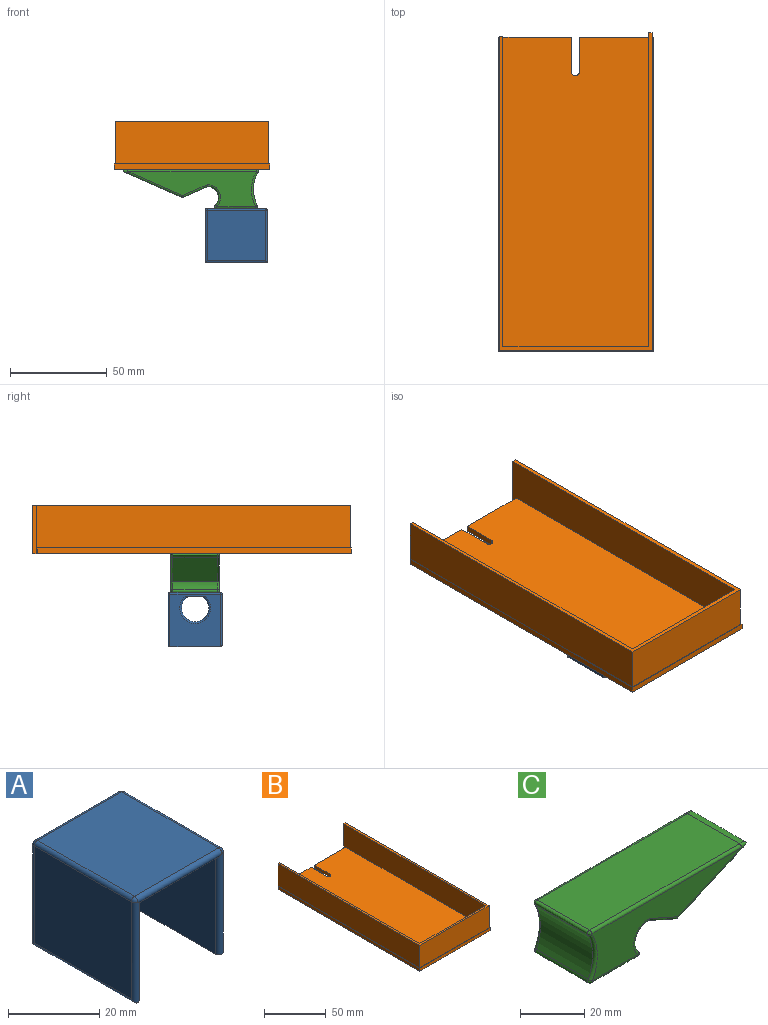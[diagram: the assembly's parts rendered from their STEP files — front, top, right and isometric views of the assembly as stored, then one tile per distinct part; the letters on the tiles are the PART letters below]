
ASSEMBLY  parts=3 mates=2
PART A: 25 faces, bbox 28x32x28.1 mm
  f0: plane 27x26mm, normal (0,1,0), area 513.9mm2, adj f1,f5,f10,f15,f20,f21
  f1: plane 32x27mm, normal (0,0,-1), area 167.1mm2, adj f0,f2,f3,f4,f6,f12,f13,f16
  f2: plane 26x24mm, normal (0,-1,0), area 435.9mm2, adj f1,f3,f4,f5,f11
  f3: plane 28x26mm, normal (1,0,0), area 728mm2, adj f1,f2,f5,f13
  f4: plane 28x26mm, normal (-1,0,0), area 728mm2, adj f1,f2,f5,f16
  f5: plane 31x24mm, normal (0,0,-1), area 693.7mm2, adj f0,f2,f3,f4,f9,f10,f11,f17
  f6: plane 30x27mm, normal (1,0,0), area 810mm2, adj f1,f16,f21,f24
  f7: plane 30x26mm, normal (0,0,1), area 780mm2, adj f14,f17,f20,f24
  f8: plane 30x26mm, normal (-1,0,0), area 780mm2, adj f12,f13,f14,f15
  f9: cylinder r=7mm len=14mm, axis (0,-1,0), area 37mm2, adj f5,f10,f11
  f10: torus R=8mm, axis (0,-1,0), area 59.3mm2, adj f0,f5,f9
  f11: torus R=8mm, axis (0,-1,0), area 59.3mm2, adj f2,f5,f9
  f12: cylinder r=1mm len=32mm, axis (0,1,0), area 49.1mm2, adj f1,f8,f13,f15
  f13: cylinder r=1mm len=27mm, axis (0,0,-1), area 83.3mm2, adj f1,f3,f8,f12,f17,f18
  f14: cylinder r=1mm len=30mm, axis (0,-1,0), area 47.1mm2, adj f7,f8,f18,f19
  f15: cylinder r=1mm len=27mm, axis (0,0,-1), area 41.8mm2, adj f0,f8,f12,f19
  f16: cylinder r=1mm len=27mm, axis (0,0,1), area 83.8mm2, adj f1,f4,f6,f17,f22
  f17: cylinder r=1mm len=26mm, axis (-1,0,0), area 79.7mm2, adj f5,f7,f13,f16,f18,f22
  f18: sphere r=1mm, area 1.6mm2, adj f13,f14,f17
  f19: sphere r=1mm, area 1.6mm2, adj f14,f15,f20
  f20: cylinder r=1mm len=26mm, axis (-1,0,0), area 40.8mm2, adj f0,f7,f19,f23
  f21: cylinder r=1mm len=27mm, axis (0,0,1), area 42.4mm2, adj f0,f1,f6,f23
  f22: sphere r=1mm, area 1.6mm2, adj f16,f17,f24
  f23: sphere r=1mm, area 1.6mm2, adj f20,f21,f24
  f24: cylinder r=1mm len=30mm, axis (0,1,0), area 47.1mm2, adj f6,f7,f22,f23
PART B: 22 faces, bbox 80x164.5x25 mm
  f0: plane 35.36x3mm, normal (0,1,0), area 106.1mm2, adj f3,f9,f15,f20
  f1: plane 35.64x3mm, normal (0,1,0), area 106.9mm2, adj f3,f9,f13,f21
  f2: plane 3x0.33mm, normal (0,1,0), area 1mm2, adj f5,f8,f9,f17
  f3: plane 159.54x75mm, normal (0,0,1), area 11887.6mm2, adj f0,f1,f13,f14,f15,f19,f20,f21
  f4: plane 3x0.67mm, normal (0,1,0), area 2mm2, adj f7,f8,f9,f11
  f5: plane 162x3mm, normal (-1,0,0), area 486mm2, adj f2,f6,f8,f9
  f6: plane 80x3mm, normal (0,-1,0), area 240mm2, adj f5,f7,f8,f9
  f7: plane 162x3mm, normal (1,0,0), area 486mm2, adj f4,f6,f8,f9
  f8: plane 162x80mm, normal (0,0,1), area 198.6mm2, adj f2,f4,f5,f6,f7,f10,f11,f17
  f9: plane 164.46x80mm, normal (0,0,-1), area 12888.2mm2, adj f0,f1,f2,f4,f5,f6,f7,f11
  f10: plane 79x22mm, normal (0,-1,0), area 1738mm2, adj f8,f11,f17,f18
  f11: plane 164x25mm, normal (1,0,0), area 3615.4mm2, adj f4,f8,f9,f10,f12,f18
  f12: plane 25x2mm, normal (0,1,0), area 50mm2, adj f9,f11,f13,f18
  f13: plane 162x25mm, normal (-1,0,0), area 3571.4mm2, adj f1,f3,f9,f12,f14,f18
  f14: plane 75x22mm, normal (0,1,0), area 1650mm2, adj f3,f13,f15,f18
  f15: plane 160x25mm, normal (1,0,0), area 3521.4mm2, adj f0,f3,f9,f14,f16,f18
  f16: plane 25x2mm, normal (0,1,0), area 50mm2, adj f9,f15,f17,f18
  f17: plane 162x25mm, normal (-1,0,0), area 3565.4mm2, adj f2,f8,f9,f10,f16,f18
  f18: plane 164x79mm, normal (0,0,1), area 802mm2, adj f10,f11,f12,f13,f14,f15,f16,f17
  f19: cylinder r=2mm len=4mm, axis (0,0,-1), area 18.8mm2, adj f3,f9,f20,f21
  f20: plane 17.84x3mm, normal (1,0,0), area 53.5mm2, adj f0,f3,f9,f19
  f21: plane 17.84x3mm, normal (-1,0,0), area 53.5mm2, adj f1,f3,f9,f19
PART C: 35 faces, bbox 76.9x26.5x21.1 mm
  f0: plane 66.1x18.01mm, normal (0,-1,0), area 654.1mm2, adj f14,f15,f20,f21,f23,f24
  f1: plane 66.1x18.01mm, normal (0,1,0), area 654.1mm2, adj f8,f10,f11,f12,f17,f18
  f2: plane 23x20.07mm, normal (0,0,-1), area 461.7mm2, adj f12,f13,f19,f20
  f3: plane 28.25x23mm, normal (0.4,0,-0.92), area 708.9mm2, adj f16,f17,f21,f22
  f4: plane 66.09x23mm, normal (0,0,1), area 1520.1mm2, adj f9,f10,f15,f16
  f5: cylinder r=18.16mm len=23mm, axis (0,1,0), area 408.5mm2, adj f8,f9,f13,f14
  f6: cylinder r=5.64mm len=23mm, axis (0,1,0), area 304.4mm2, adj f7,f11,f19,f23
  f7: plane 23x12.38mm, normal (-0.41,0,-0.91), area 311.8mm2, adj f6,f18,f22,f24
  f8: bspline ~18x3.24mm, area 29.4mm2, adj f1,f5,f25,f26
  f9: bspline ~26.5x1.48mm, area 54.2mm2, adj f4,f5,f25,f27
  f10: bspline ~76.86x1mm, area 107.5mm2, adj f1,f4,f25,f28
  f11: bspline ~11.29x6.86mm, area 23mm2, adj f1,f6,f18,f29
  f12: bspline ~27.18x1mm, area 32.6mm2, adj f1,f2,f26,f29
  f13: bspline ~26.5x1.46mm, area 53.1mm2, adj f2,f5,f26,f30
  f14: bspline ~18x3.24mm, area 29.4mm2, adj f0,f5,f27,f30
  f15: bspline ~76.86x1mm, area 107.5mm2, adj f0,f4,f27,f31
  f16: bspline ~26.5x2.85mm, area 121.1mm2, adj f3,f4,f28,f31
  f17: bspline ~34.95x15.99mm, area 50.1mm2, adj f1,f3,f28,f32
  f18: bspline ~14.3x7.12mm, area 22.2mm2, adj f1,f7,f11,f32
  f19: bspline ~26.5x1.7mm, area 69.2mm2, adj f2,f6,f29,f33
  f20: bspline ~27.18x1mm, area 32.6mm2, adj f0,f2,f30,f33
  f21: bspline ~34.95x15.99mm, area 50.1mm2, adj f0,f3,f31,f34
  f22: bspline ~26.5x0.81mm, area 19.2mm2, adj f3,f7,f32,f34
  f23: bspline ~11.29x6.86mm, area 23mm2, adj f0,f6,f24,f33
  f24: bspline ~14.3x7.12mm, area 22.2mm2, adj f0,f7,f23,f34
  f25: bspline ~1.87x1.58mm, area 1.4mm2, adj f8,f9,f10
  f26: bspline ~1.86x1.61mm, area 1.4mm2, adj f8,f12,f13
  f27: bspline ~1.86x1.6mm, area 1.3mm2, adj f9,f14,f15
  f28: bspline ~2.98x2.59mm, area 5.8mm2, adj f10,f16,f17
  f29: bspline ~1.9x1.81mm, area 3mm2, adj f11,f12,f19
  f30: bspline ~1.85x1.61mm, area 1.4mm2, adj f13,f14,f20
  f31: bspline ~2.98x2.61mm, area 5.9mm2, adj f15,f16,f21
  f32: bspline ~1.16x1.06mm, area 0.7mm2, adj f17,f18,f22
  f33: bspline ~1.9x1.81mm, area 3mm2, adj f19,f20,f23
  f34: bspline ~1.17x1.06mm, area 0.7mm2, adj f21,f22,f24
PLACE A rot(axis=(0,0,1),90deg) t=(-9.91,3.46,-102.4)mm
PLACE B t=(-31.45,-40.6,-120.38)mm
PLACE C rot(axis=(0,0,1),180deg) t=(8.58,-0.41,-140.38)mm
MATE fastened A.f7 <-> C.f2  axis (0,0,1) through (6.09,12.09,-140.38)mm
MATE fastened B.f9 <-> C.f4  axis (0,0,-1) through (-16.68,12.09,-120.38)mm
